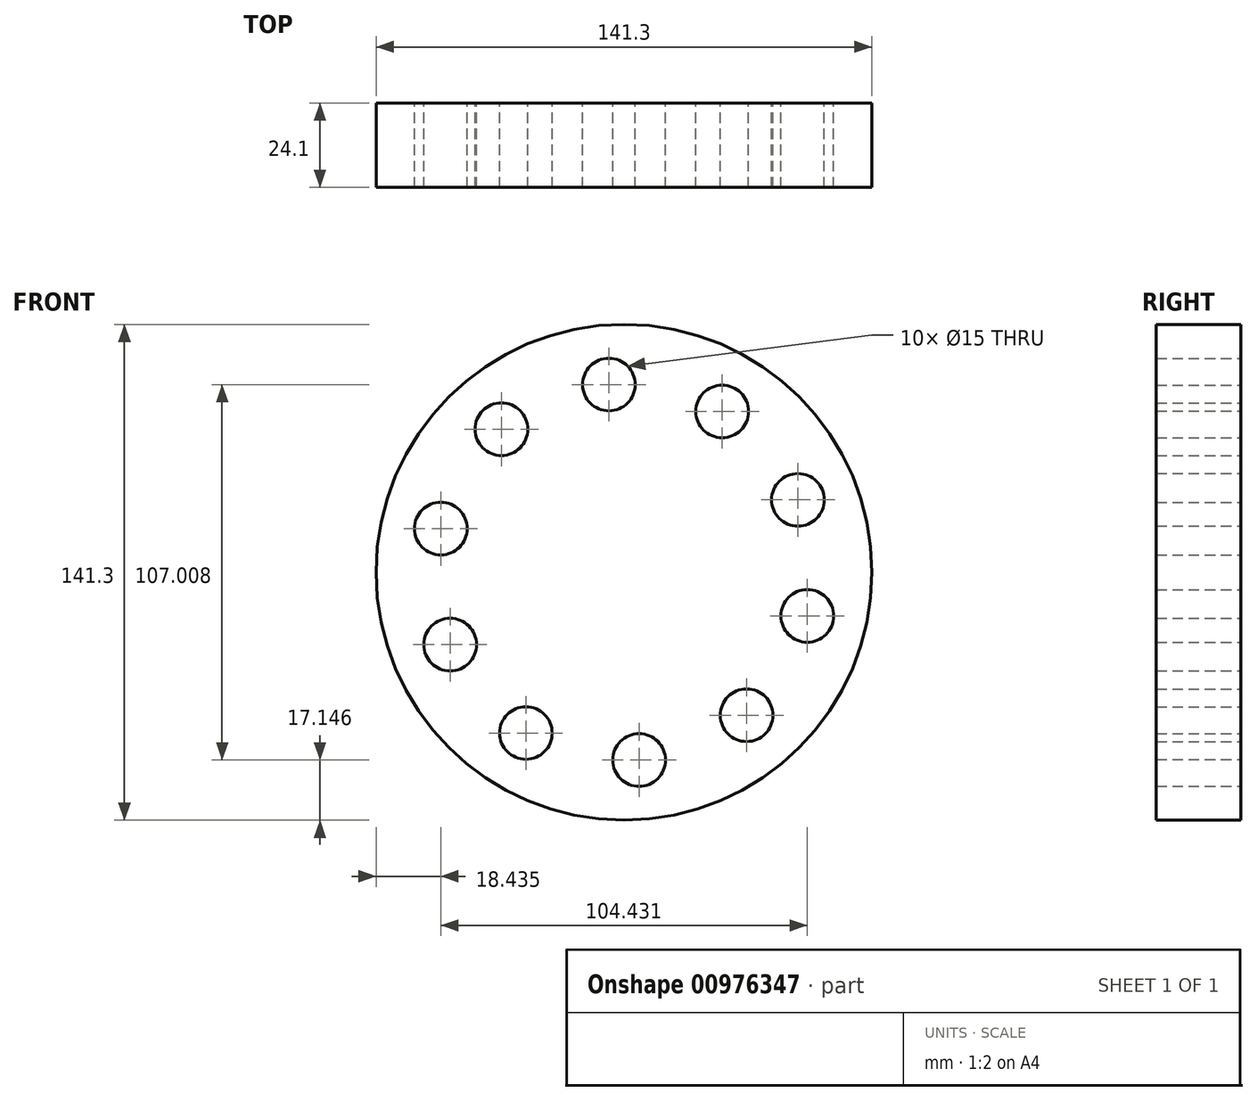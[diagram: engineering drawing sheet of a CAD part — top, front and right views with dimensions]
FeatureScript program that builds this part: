
annotation { "Feature Type Name" : "Feature", "Feature Type Description" : "" }
export const myFeature = defineFeature(function(context is Context, id is Id, definition is map)
    precondition{}
    {
        {
            var Q0;
            Q0=qCreatedBy(makeId("Front.planeOp"),FACE);
            var sketch = newSketch(context, id + "F0", { "sketchPlane" : qUnion([Q0])});
            skCircle(sketch, "E0", {"center": v(0, 0) * mm, "radius": 70.65 * mm});
            skCircle(sketch, "E1", {"center": v(-34.93, 40.76) * mm, "radius": 7.5 * mm});
            skCircle(sketch, "E2.1.0", {"center": v(-52.22, 12.44) * mm, "radius": 7.5 * mm});
            skCircle(sketch, "E2.2.0", {"center": v(-49.56, -20.63) * mm, "radius": 7.5 * mm});
            skCircle(sketch, "E2.3.0", {"center": v(-27.97, -45.82) * mm, "radius": 7.5 * mm});
            skCircle(sketch, "E2.4.0", {"center": v(4.3, -53.5) * mm, "radius": 7.5 * mm});
            skCircle(sketch, "E2.5.0", {"center": v(34.93, -40.76) * mm, "radius": 7.5 * mm});
            skCircle(sketch, "E2.6.0", {"center": v(52.22, -12.44) * mm, "radius": 7.5 * mm});
            skCircle(sketch, "E2.7.0", {"center": v(49.56, 20.63) * mm, "radius": 7.5 * mm});
            skCircle(sketch, "E2.8.0", {"center": v(27.97, 45.82) * mm, "radius": 7.5 * mm});
            skCircle(sketch, "E2.9.0", {"center": v(-4.3, 53.5) * mm, "radius": 7.5 * mm});
            skSolve(sketch);
        }
        {
            var Q0;
            Q0=makeQuery(id+"F0.imprint","IMPRINT",FACE,{"disambiguationData":[TD([[makeQuery(id+"F0.imprint","IMPRINT",EDGE,{"derivedFrom":sQuery(id+"F0.wireOp",EDGE,"E0")}),1.0]])]});
            extrude(context, id + "F1", {"entities" : qUnion([Q0]), "depth" : 24.1 * mm, "offsetDistance" : 25 * mm});
        }
    });
